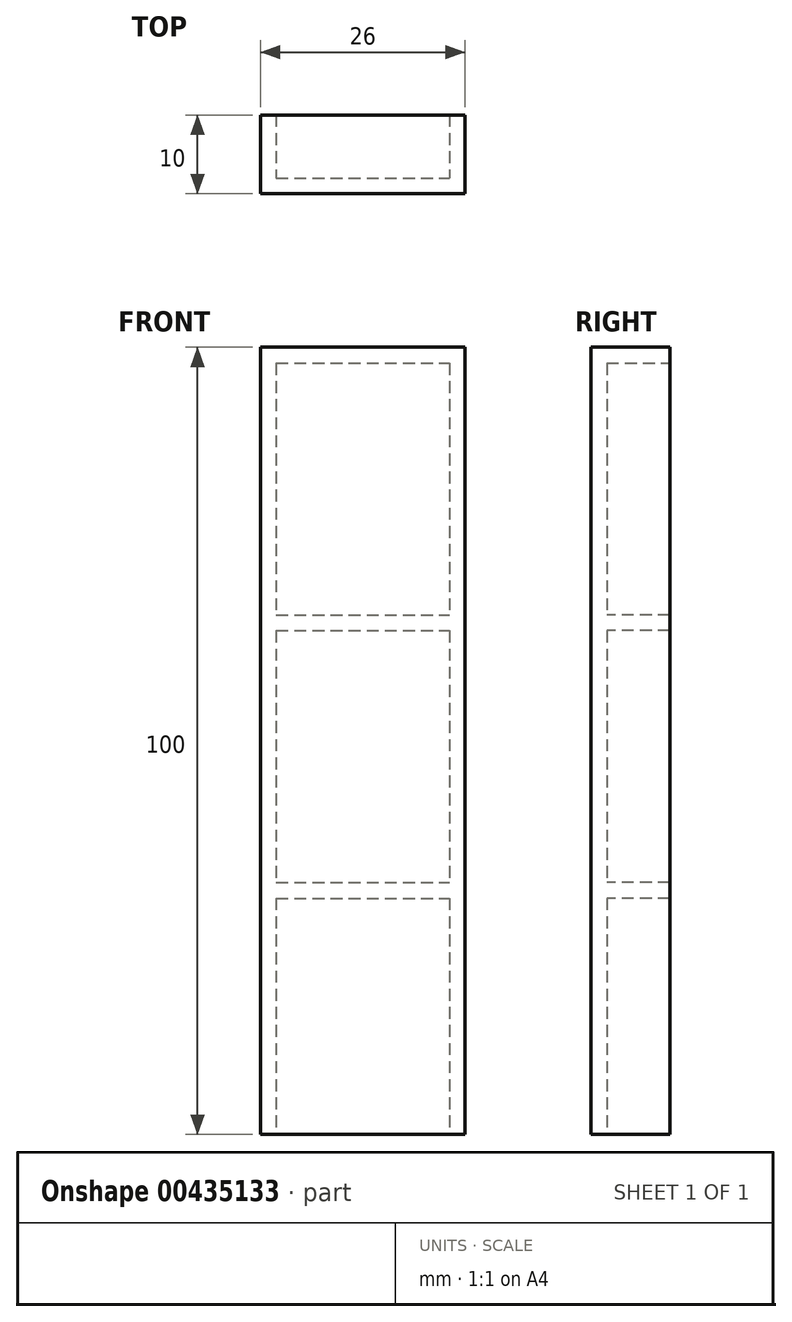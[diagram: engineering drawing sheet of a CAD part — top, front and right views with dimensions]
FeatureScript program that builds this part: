
annotation { "Feature Type Name" : "Feature", "Feature Type Description" : "" }
export const myFeature = defineFeature(function(context is Context, id is Id, definition is map)
    precondition{}
    {
        {
            var Q0;
            Q0=qCreatedBy(makeId("Top.planeOp"),FACE);
            var sketch = newSketch(context, id + "F0", { "sketchPlane" : qUnion([Q0])});
            skLineSegment(sketch, "E0", {"start": v(0, 0) * mm, "end": v(0, -10) * mm});
            skLineSegment(sketch, "E1", {"start": v(0, -10) * mm, "end": v(26, -10) * mm});
            skLineSegment(sketch, "E2", {"start": v(26, -10) * mm, "end": v(26, 0) * mm});
            skLineSegment(sketch, "E3.0", {"start": v(2, 0) * mm, "end": v(2, -8) * mm});
            skLineSegment(sketch, "E4.0", {"start": v(2, -8) * mm, "end": v(24, -8) * mm});
            skLineSegment(sketch, "E5.0", {"start": v(24, -8) * mm, "end": v(24, 0) * mm});
            skLineSegment(sketch, "E6", {"start": v(0, 0) * mm, "end": v(2, 0) * mm});
            skLineSegment(sketch, "E7", {"start": v(24, 0) * mm, "end": v(26, 0) * mm});
            skSolve(sketch);
        }
        {
            var Q0;
            Q0=makeQuery(id+"F0.imprint","IMPRINT",FACE,{"disambiguationData":[TD([[makeQuery(id+"F0.imprint","IMPRINT",EDGE,{"derivedFrom":sQuery(id+"F0.wireOp",EDGE,"E0")}),1.0]])]});
            extrude(context, id + "F1", {"entities" : qUnion([Q0]), "depth" : 98 * mm});
        }
        {
            var Q0;
            Q0=makeQuery(id+"F1.opExtrude","CAP_FACE",FACE,{"disambiguationData":[OSD([sQuery(id+"F0.wireOp",EDGE,"E0"),sQuery(id+"F0.wireOp",EDGE,"E1"),sQuery(id+"F0.wireOp",EDGE,"E2"),sQuery(id+"F0.wireOp",EDGE,"E3.0"),sQuery(id+"F0.wireOp",EDGE,"E4.0"),sQuery(id+"F0.wireOp",EDGE,"E5.0"),sQuery(id+"F0.wireOp",EDGE,"E6"),sQuery(id+"F0.wireOp",EDGE,"E7")])],"isStart":false});
            var sketch = newSketch(context, id + "F2", { "sketchPlane" : qUnion([Q0])});
            skLineSegment(sketch, "E8.bottom", {"start": v(0, 0) * mm, "end": v(26, 0) * mm});
            skLineSegment(sketch, "E8.top", {"start": v(0, -10) * mm, "end": v(26, -10) * mm});
            skLineSegment(sketch, "E8.left", {"start": v(0, 0) * mm, "end": v(0, -10) * mm});
            skLineSegment(sketch, "E8.right", {"start": v(26, 0) * mm, "end": v(26, -10) * mm});
            skSolve(sketch);
        }
        {
            var Q0;
            Q0 = qSketchRegion(id + "F2", true);
            extrude(context, id + "F3", {"entities" : qUnion([Q0]), "operationType" : NewBodyOperationType.ADD, "depth" : 2 * mm});
        }
        {
            var Q0;
            Q0=makeQuery(id+"F1.opExtrude","SWEPT_FACE",FACE,{"disambiguationData":[OSD([sQuery(id+"F0.wireOp",EDGE,"E4.0")])]});
            var sketch = newSketch(context, id + "F4", { "sketchPlane" : qUnion([Q0])});
            skLineSegment(sketch, "E9.bottom", {"start": v(-2, 66) * mm, "end": v(-24, 66) * mm});
            skLineSegment(sketch, "E9.top", {"start": v(-2, 64) * mm, "end": v(-24, 64) * mm});
            skLineSegment(sketch, "E9.left", {"start": v(-2, 66) * mm, "end": v(-2, 64) * mm});
            skLineSegment(sketch, "E9.right", {"start": v(-24, 66) * mm, "end": v(-24, 64) * mm});
            skLineSegment(sketch, "E10.bottom", {"start": v(-2, 32) * mm, "end": v(-24, 32) * mm});
            skLineSegment(sketch, "E10.top", {"start": v(-2, 30) * mm, "end": v(-24, 30) * mm});
            skLineSegment(sketch, "E10.left", {"start": v(-2, 32) * mm, "end": v(-2, 30) * mm});
            skLineSegment(sketch, "E10.right", {"start": v(-24, 32) * mm, "end": v(-24, 30) * mm});
            skSolve(sketch);
        }
        {
            var Q0;
            Q0 = qSketchRegion(id + "F4", true);
            var Q1;
            Q1=makeQuery(id+"F3.boolean.opBoolean","MERGE",FACE,{"derivedFrom":[makeQuery(id+"F1.opExtrude","SWEPT_FACE",FACE,{"disambiguationData":[OSD([sQuery(id+"F0.wireOp",EDGE,"E6")])]}),makeQuery(id+"F1.opExtrude","SWEPT_FACE",FACE,{"disambiguationData":[OSD([sQuery(id+"F0.wireOp",EDGE,"E7")])]}),makeQuery(id+"F3.opExtrude","SWEPT_FACE",FACE,{"disambiguationData":[OSD([sQuery(id+"F2.wireOp",EDGE,"E8.bottom")])]})]});
            extrude(context, id + "F5", {"entities" : qUnion([Q0]), "operationType" : NewBodyOperationType.ADD, "endBound" : BoundingType.UP_TO_SURFACE, "endBoundEntityFace" : qUnion([Q1]), "depth" : 25 * mm});
        }
    });
